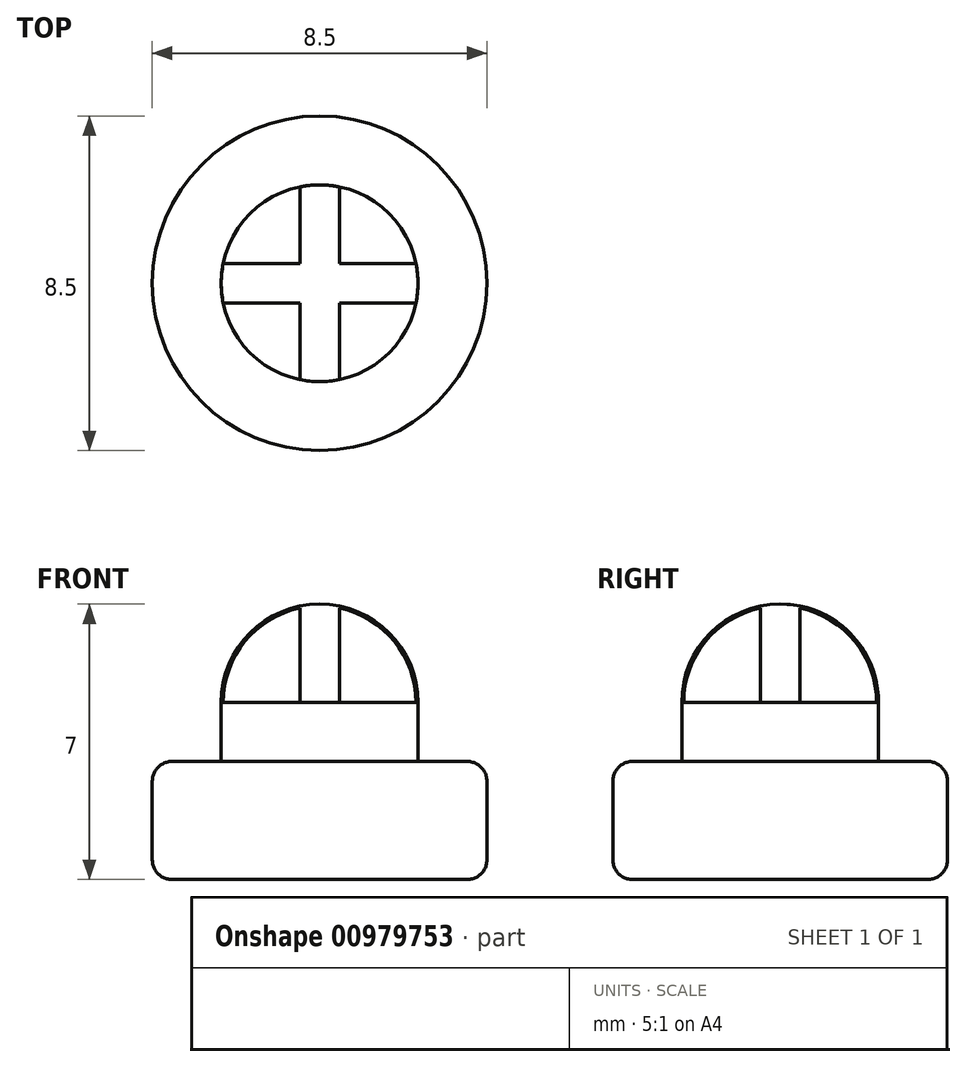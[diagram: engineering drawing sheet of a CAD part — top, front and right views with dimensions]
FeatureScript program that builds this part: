
annotation { "Feature Type Name" : "Feature", "Feature Type Description" : "" }
export const myFeature = defineFeature(function(context is Context, id is Id, definition is map)
    precondition{}
    {
        {
            var Q0;
            Q0=qCreatedBy(makeId("Top.planeOp"),FACE);
            var sketch = newSketch(context, id + "F0", { "sketchPlane" : qUnion([Q0])});
            skCircle(sketch, "E0", {"center": v(0, 0) * mm, "radius": 4.25 * mm});
            skSolve(sketch);
        }
        {
            var Q0;
            Q0 = qSketchRegion(id + "F0", true);
            extrude(context, id + "F1", {"entities" : qUnion([Q0]), "depth" : 3 * mm, "offsetDistance" : 25 * mm});
        }
        {
            var Q0;
            Q0=makeQuery(id+"F1.opExtrude","CAP_FACE",FACE,{"disambiguationData":[OSD([sQuery(id+"F0.wireOp",EDGE,"E0")])],"isStart":false});
            var sketch = newSketch(context, id + "F2", { "sketchPlane" : qUnion([Q0])});
            skCircle(sketch, "E1", {"center": v(0, 0) * mm, "radius": 2.5 * mm});
            skSolve(sketch);
        }
        {
            var Q0;
            Q0 = qSketchRegion(id + "F2", true);
            extrude(context, id + "F3", {"entities" : qUnion([Q0]), "operationType" : NewBodyOperationType.ADD, "depth" : 1.5 * mm, "offsetDistance" : 25 * mm});
        }
        {
            var Q0;
            Q0=qCreatedBy(makeId("Right.planeOp"),FACE);
            var sketch = newSketch(context, id + "F4", { "sketchPlane" : qUnion([Q0])});
            skLineSegment(sketch, "E2", {"start": v(0, 4.5) * mm, "end": v(-2.5, 4.5) * mm});
            skArc(sketch, "E3", {"start": v(0, 7) * mm, "mid": v(-1.77, 6.27) * mm, "end": v(-2.5, 4.5) * mm});
            skLineSegment(sketch, "E4", {"start": v(0, 7) * mm, "end": v(0, 4.5) * mm});
            skSolve(sketch);
        }
        {
            var Q0;
            Q0=makeQuery(id+"F4.imprint","IMPRINT",FACE,{"disambiguationData":[TD([[makeQuery(id+"F4.imprint","IMPRINT",EDGE,{"derivedFrom":sQuery(id+"F4.wireOp",EDGE,"E2")}),-1.0]])]});
            var Q1;
            Q1=sQuery(id+"F4.wireOp",EDGE,"E4");
            revolve(context, id + "F5", {"surfaceOperationType" : NewSurfaceOperationType.NEW, "entities" : qUnion([Q0]), "axis" : qUnion([Q1]), "revolveType" : RevolveType.FULL});
        }
        {
            var Q0;
            Q0=makeQuery(id+"F3.opExtrude","CAP_FACE",FACE,{"disambiguationData":[OSD([sQuery(id+"F2.wireOp",EDGE,"E1")])],"isStart":false});
            var sketch = newSketch(context, id + "F6", { "sketchPlane" : qUnion([Q0])});
            skLineSegment(sketch, "E5.bottom", {"start": v(0.5, -0.5) * mm, "end": v(3.5, -0.5) * mm});
            skLineSegment(sketch, "E5.top", {"start": v(0.5, -3.5) * mm, "end": v(3.5, -3.5) * mm});
            skLineSegment(sketch, "E5.left", {"start": v(0.5, -0.5) * mm, "end": v(0.5, -3.5) * mm});
            skLineSegment(sketch, "E5.right", {"start": v(3.5, -0.5) * mm, "end": v(3.5, -3.5) * mm});
            skSolve(sketch);
        }
        {
            var Q0;
            {var subQ2=sQuery(id+"F6.wireOp",EDGE,"E5.top");Q0=makeQuery(id+"F6.imprint","IMPRINT",FACE,{"disambiguationData":[TD([[makeQuery(id+"F6.imprint","IMPRINT",EDGE,{"derivedFrom":subQ2}),1.0]])]});}
            var Q1;
            {var subQ0=sQuery(id+"F6.wireOp",EDGE,"E5.left");var subQ1=sQuery(id+"F6.wireOp",EDGE,"E5.bottom");var subQ2=makeQuery(id+"F6.imprint","INTERSECT",VERTEX,{"derivedFrom":[subQ1,subQ0]});Q1=makeQuery(id+"F6.imprint","IMPRINT",FACE,{"disambiguationData":[TD([[makeQuery(id+"F6.imprint","IMPRINT",EDGE,{"disambiguationData":[TD([[subQ2,-1.0]])],"derivedFrom":subQ1}),-1.0]])]});}
            extrude(context, id + "F7", {"entities" : qUnion([Q0, Q1]), "depth" : 25 * mm, "offsetDistance" : 25 * mm});
        }
        {
            var Q0;
            Q0=makeQuery(id+"F7.opExtrude","SWEPT_BODY",BODY,{"disambiguationData":[OSD([sQuery(id+"F6.wireOp",EDGE,"E5.bottom"),sQuery(id+"F6.wireOp",EDGE,"E5.top"),sQuery(id+"F6.wireOp",EDGE,"E5.left"),sQuery(id+"F6.wireOp",EDGE,"E5.right")])]});
            var Q1;
            Q1=sQuery(id+"F4.wireOp",EDGE,"E4");
            circularPattern(context, id + "F8", {"entities" : qUnion([Q0]), "axis" : qUnion([Q1]), "angle" : 360 * degree, "instanceCount" : 4, "equalSpace" : true});
        }
        {
            var Q0;
            Q0=makeQuery(id+"F8.opPattern","COPY",BODY,{"derivedFrom":makeQuery(id+"F7.opExtrude","SWEPT_BODY",BODY,{"disambiguationData":[OSD([sQuery(id+"F6.wireOp",EDGE,"E5.bottom"),sQuery(id+"F6.wireOp",EDGE,"E5.top"),sQuery(id+"F6.wireOp",EDGE,"E5.left"),sQuery(id+"F6.wireOp",EDGE,"E5.right")])]}),"instanceName":"1"});
            var Q1;
            Q1=makeQuery(id+"F8.opPattern","COPY",BODY,{"derivedFrom":makeQuery(id+"F7.opExtrude","SWEPT_BODY",BODY,{"disambiguationData":[OSD([sQuery(id+"F6.wireOp",EDGE,"E5.bottom"),sQuery(id+"F6.wireOp",EDGE,"E5.top"),sQuery(id+"F6.wireOp",EDGE,"E5.left"),sQuery(id+"F6.wireOp",EDGE,"E5.right")])]}),"instanceName":"2"});
            var Q2;
            Q2=makeQuery(id+"F8.opPattern","COPY",BODY,{"derivedFrom":makeQuery(id+"F7.opExtrude","SWEPT_BODY",BODY,{"disambiguationData":[OSD([sQuery(id+"F6.wireOp",EDGE,"E5.bottom"),sQuery(id+"F6.wireOp",EDGE,"E5.top"),sQuery(id+"F6.wireOp",EDGE,"E5.left"),sQuery(id+"F6.wireOp",EDGE,"E5.right")])]}),"instanceName":"3"});
            var Q3;
            Q3=makeQuery(id+"F7.opExtrude","SWEPT_BODY",BODY,{"disambiguationData":[OSD([sQuery(id+"F6.wireOp",EDGE,"E5.bottom"),sQuery(id+"F6.wireOp",EDGE,"E5.top"),sQuery(id+"F6.wireOp",EDGE,"E5.left"),sQuery(id+"F6.wireOp",EDGE,"E5.right")])]});
            var Q4;
            Q4=makeQuery(id+"F5.opRevolve","SWEPT_BODY",BODY,{"disambiguationData":[OSD([sQuery(id+"F4.wireOp",EDGE,"E2"),sQuery(id+"F4.wireOp",EDGE,"E3"),sQuery(id+"F4.wireOp",EDGE,"E4")])]});
            booleanBodies(context, id + "F9", {"operationType" : BooleanOperationType.SUBTRACTION, "tools" : qUnion([Q0, Q1, Q2, Q3]), "targets" : qUnion([Q4])});
        }
        {
            var Q0;
            Q0=makeQuery(id+"F1.opExtrude","CAP_EDGE",EDGE,{"disambiguationData":[OSD([sQuery(id+"F0.wireOp",EDGE,"E0")])],"isStart":false});
            var Q1;
            Q1=makeQuery(id+"F1.opExtrude","CAP_EDGE",EDGE,{"disambiguationData":[OSD([sQuery(id+"F0.wireOp",EDGE,"E0")])],"isStart":true});
            var Q2;
            Q2=makeQuery(id+"F3.opExtrude","CAP_EDGE",EDGE,{"disambiguationData":[OSD([sQuery(id+"F2.wireOp",EDGE,"E1")])],"isStart":true});
            fillet(context, id + "F10", {"entities" : qUnion([Q0, Q1, Q2]), "radius" : 0.5 * mm, "tangentPropagation" : true, "allowEdgeOverflow" : false});
        }
    });
